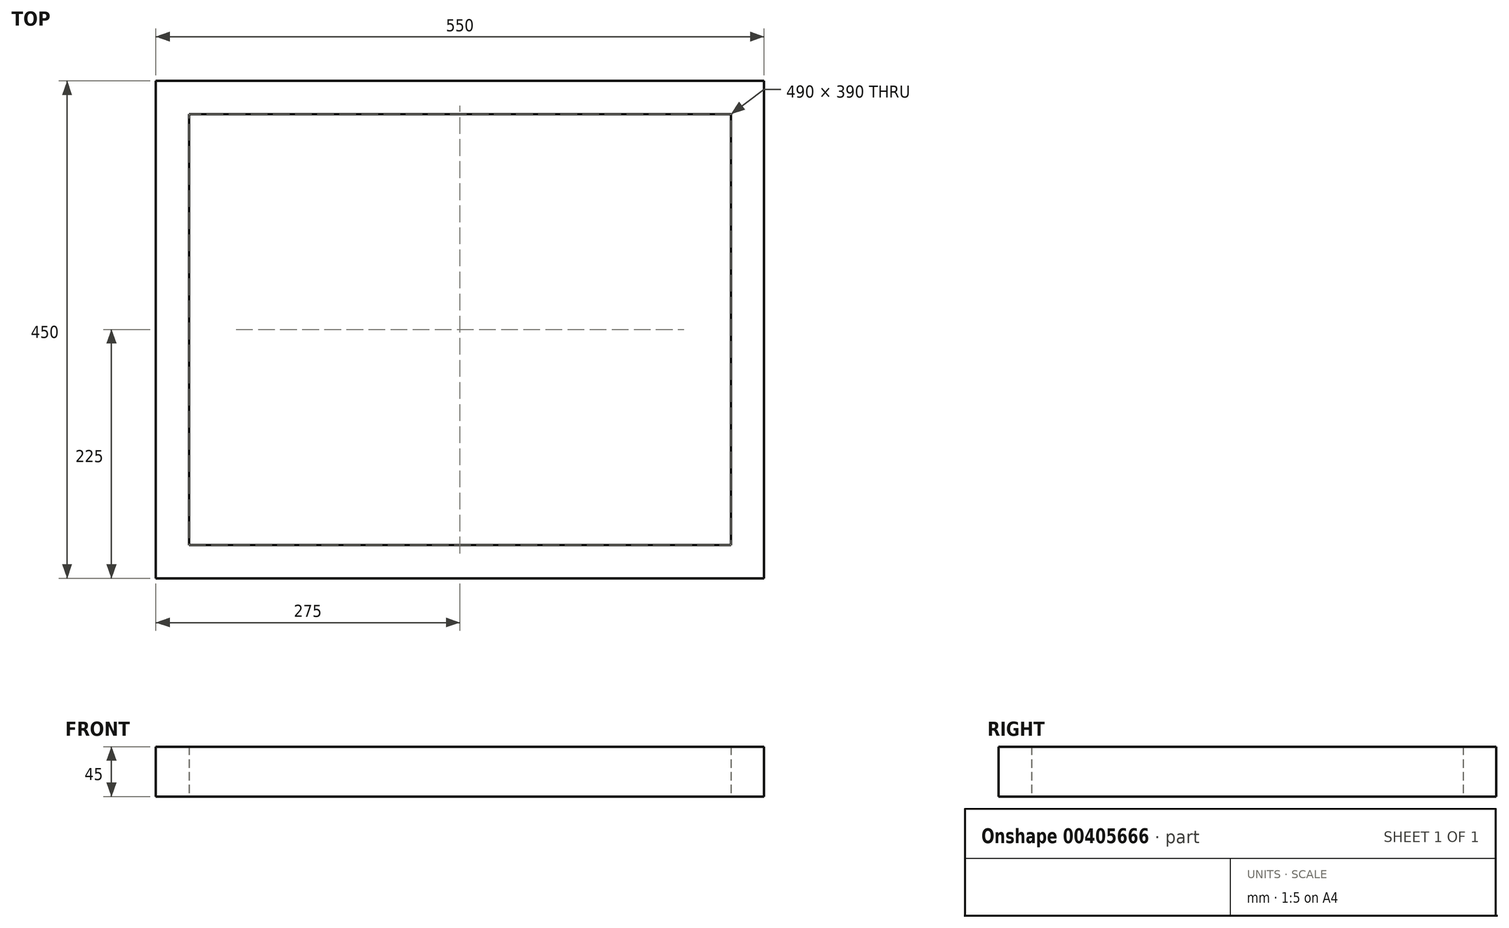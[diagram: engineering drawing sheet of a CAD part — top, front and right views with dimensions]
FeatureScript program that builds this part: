
annotation { "Feature Type Name" : "Feature", "Feature Type Description" : "" }
export const myFeature = defineFeature(function(context is Context, id is Id, definition is map)
    precondition{}
    {
        {
            var Q0;
            Q0=qCreatedBy(makeId("Top.planeOp"),FACE);
            var sketch = newSketch(context, id + "F0", { "sketchPlane" : qUnion([Q0])});
            skLineSegment(sketch, "E0.bottom", {"start": v(275, 225) * mm, "end": v(-275, 225) * mm});
            skLineSegment(sketch, "E0.top", {"start": v(275, -225) * mm, "end": v(-275, -225) * mm});
            skLineSegment(sketch, "E0.left", {"start": v(275, 225) * mm, "end": v(275, -225) * mm});
            skLineSegment(sketch, "E0.right", {"start": v(-275, 225) * mm, "end": v(-275, -225) * mm});
            skPoint(sketch, "E0.middle", {"position": v(0, 0) * mm});
            skLineSegment(sketch, "E1.bottom", {"start": v(245, 195) * mm, "end": v(-245, 195) * mm});
            skLineSegment(sketch, "E1.top", {"start": v(245, -195) * mm, "end": v(-245, -195) * mm});
            skLineSegment(sketch, "E1.left", {"start": v(245, 195) * mm, "end": v(245, -195) * mm});
            skLineSegment(sketch, "E1.right", {"start": v(-245, 195) * mm, "end": v(-245, -195) * mm});
            skSolve(sketch);
        }
        {
            var Q0;
            Q0=makeQuery(id+"F0.imprint","IMPRINT",FACE,{"disambiguationData":[TD([[makeQuery(id+"F0.imprint","IMPRINT",EDGE,{"derivedFrom":sQuery(id+"F0.wireOp",EDGE,"E0.bottom")}),1.0]])]});
            extrude(context, id + "F1", {"entities" : qUnion([Q0]), "endBound" : BoundingType.SYMMETRIC, "depth" : 45 * mm});
        }
    });
